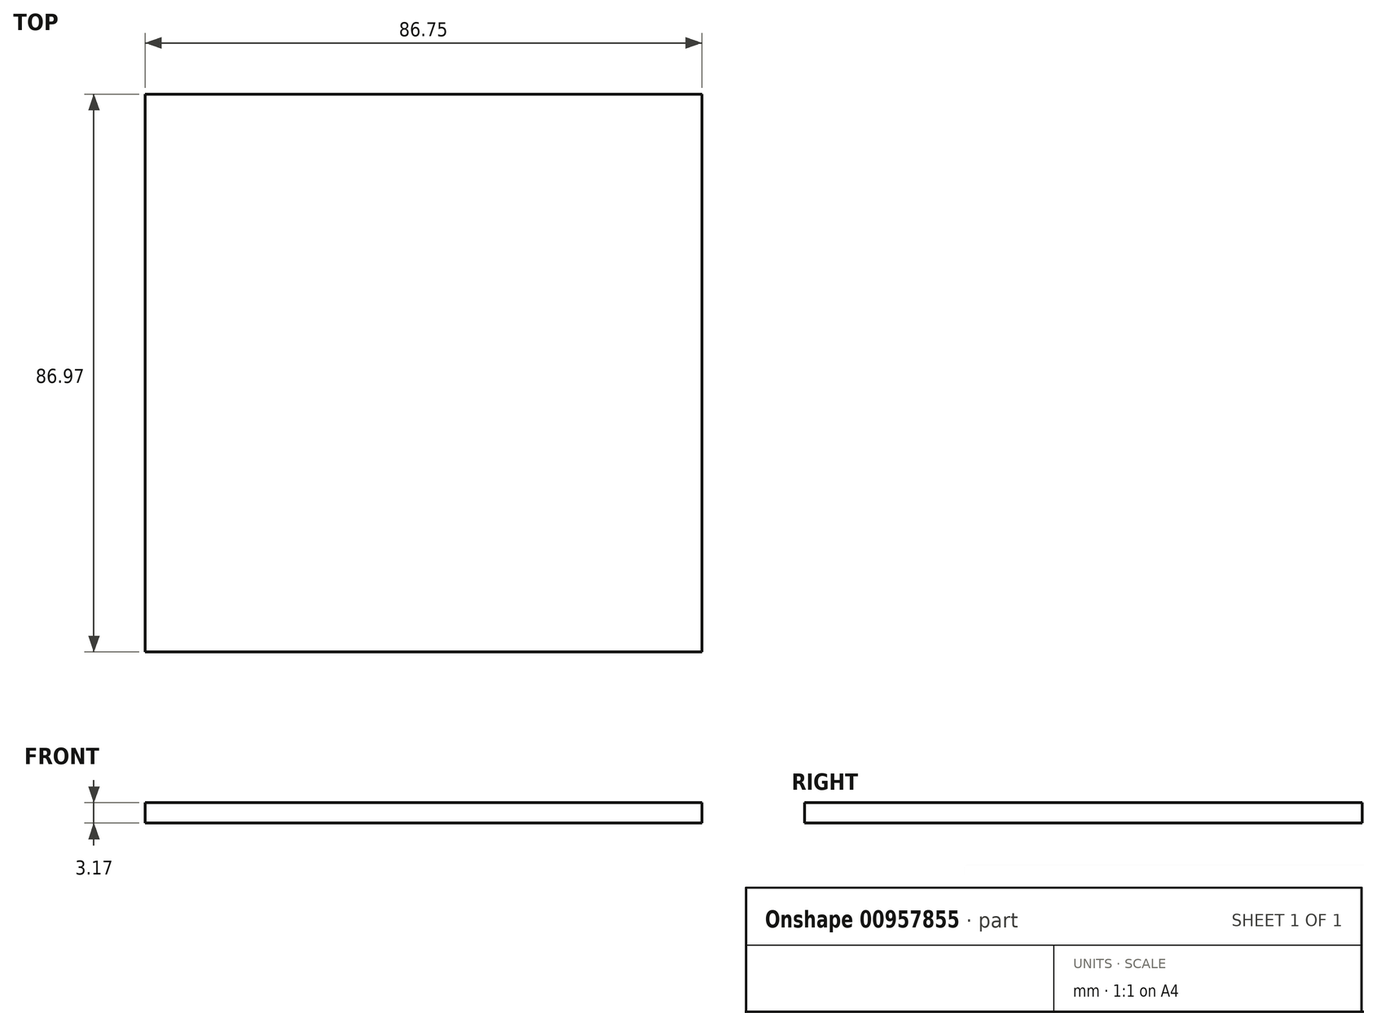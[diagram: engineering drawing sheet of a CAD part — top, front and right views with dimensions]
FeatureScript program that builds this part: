
annotation { "Feature Type Name" : "Feature", "Feature Type Description" : "" }
export const myFeature = defineFeature(function(context is Context, id is Id, definition is map)
    precondition{}
    {
        {
            var Q0;
            Q0=qCreatedBy(makeId("Top.planeOp"),FACE);
            var sketch = newSketch(context, id + "F0", { "sketchPlane" : qUnion([Q0])});
            skLineSegment(sketch, "E0.bottom", {"start": v(-49.08, -27.16) * mm, "end": v(37.67, -27.16) * mm});
            skLineSegment(sketch, "E0.top", {"start": v(-49.08, 59.81) * mm, "end": v(37.67, 59.81) * mm});
            skLineSegment(sketch, "E0.left", {"start": v(-49.08, -27.16) * mm, "end": v(-49.08, 59.81) * mm});
            skLineSegment(sketch, "E0.right", {"start": v(37.67, -27.16) * mm, "end": v(37.67, 59.81) * mm});
            skSolve(sketch);
        }
        {
            var Q0;
            Q0 = qSketchRegion(id + "F0", true);
            extrude(context, id + "F1", {"entities" : qUnion([Q0]), "depth" : 3.17 * mm, "offsetDistance" : 25.4 * mm});
        }
    });
